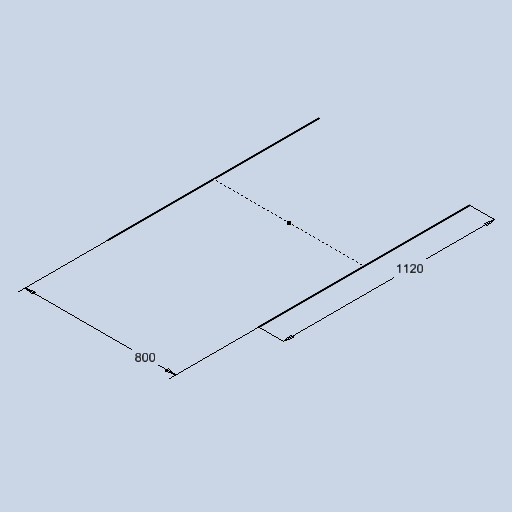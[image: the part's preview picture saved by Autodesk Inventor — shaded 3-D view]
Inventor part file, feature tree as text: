
AUTODESK INVENTOR PART (.ipt)
format: ipt  version: 2025 (Build 290162010, 162A)  size: 127,488 bytes
history: native  units: mm
features: sketch x1
ambient origin geometry x8: Origin, YZ Plane, XZ Plane, XY Plane, X Axis, Y Axis, Z Axis, Center Point
feature tree (1):
  sketch  "Sketch1"  dims[d0=1120.0mm d1=800.0mm]
